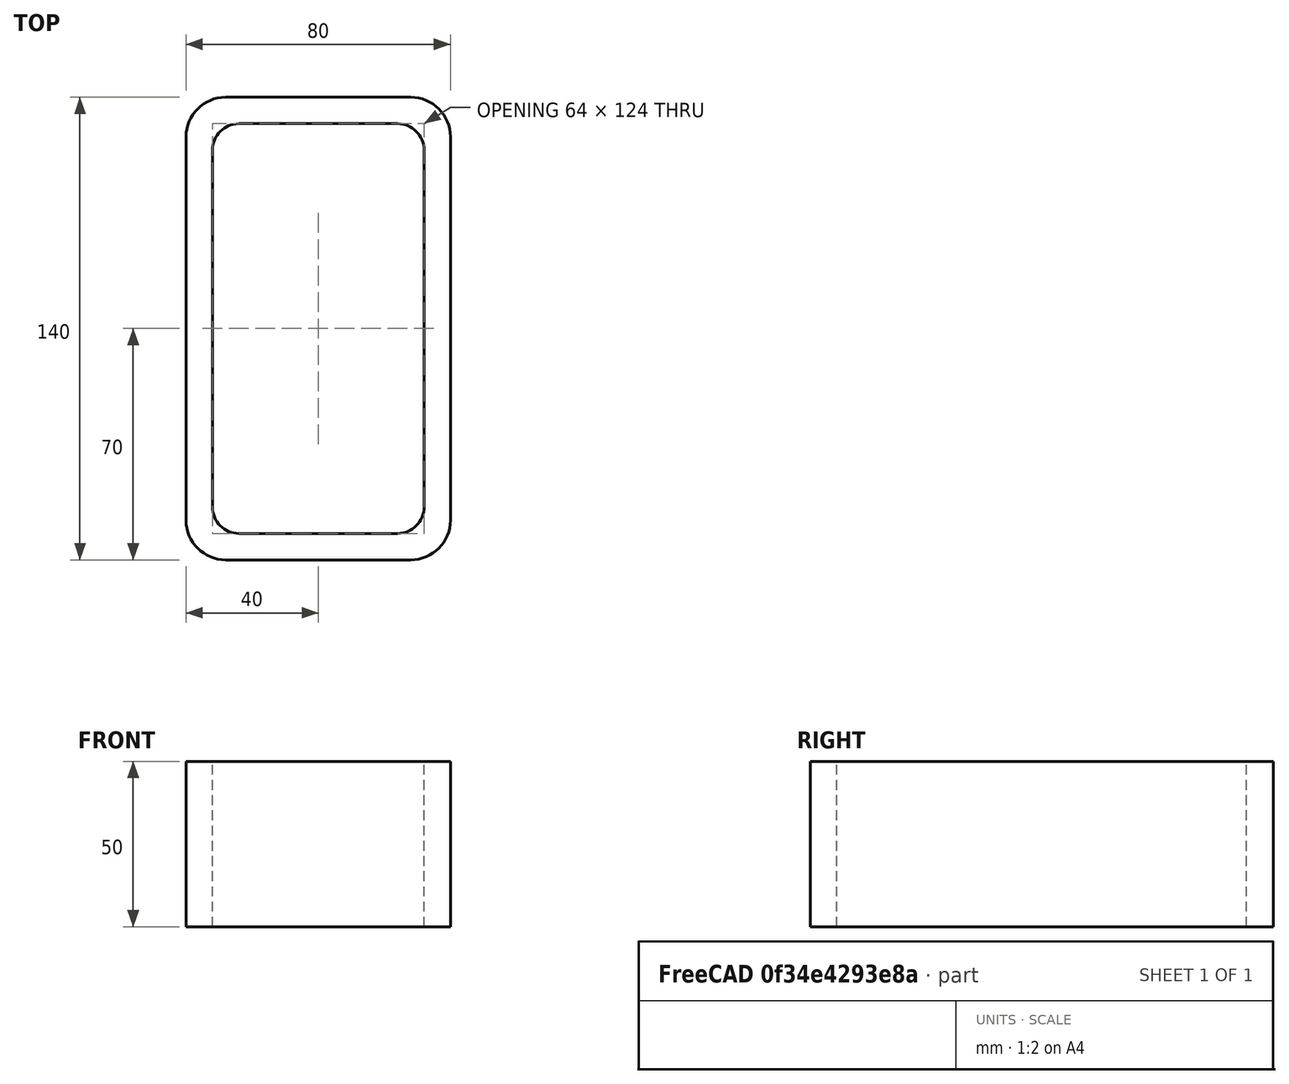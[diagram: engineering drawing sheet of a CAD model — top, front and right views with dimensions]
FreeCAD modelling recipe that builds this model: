
FCSTD DOCUMENT  (FreeCAD 0.15R4671 (Git))
Label: Rectangular hollow section 140x80x8 EN10219 S235JRH
License: All rights reserved
LicenseURL: http://en.wikipedia.org/wiki/All_rights_reserved
objects: Sketcher::SketchObject×1, Part::Extrusion×1
note: 2 computed .brp shape members not serialized (recipe doc carries the construction recipe); baked Part::Feature solids carry a one-line shape summary decoded from their .brp

FEATURE [Sketcher::SketchObject] Sketch
  sketch-geometry (16):
    g0: LineSegment StartX=-24 StartY=62 StartZ=0 EndX=24 EndY=62 EndZ=0
    g1: LineSegment StartX=32 StartY=54 StartZ=0 EndX=32 EndY=-54 EndZ=0
    g2: LineSegment StartX=24 StartY=-62 StartZ=0 EndX=-24 EndY=-62 EndZ=0
    g3: LineSegment StartX=-32 StartY=-54 StartZ=0 EndX=-32 EndY=54 EndZ=0
    g4: LineSegment StartX=-28 StartY=70 StartZ=0 EndX=28 EndY=70 EndZ=0
    g5: LineSegment StartX=40 StartY=58 StartZ=0 EndX=40 EndY=-58 EndZ=0
    g6: LineSegment StartX=28 StartY=-70 StartZ=0 EndX=-28 EndY=-70 EndZ=0
    g7: LineSegment StartX=-40 StartY=-58 StartZ=0 EndX=-40 EndY=58 EndZ=0
    g8: ArcOfCircle CenterX=-24 CenterY=54 CenterZ=0 NormalX=0 NormalY=0 NormalZ=1 Radius=8 StartAngle=1.5708 EndAngle=3.14159
    g9: ArcOfCircle CenterX=24 CenterY=54 CenterZ=0 NormalX=0 NormalY=0 NormalZ=1 Radius=8 StartAngle=0 EndAngle=1.5708
    g10: ArcOfCircle CenterX=24 CenterY=-54 CenterZ=0 NormalX=0 NormalY=0 NormalZ=1 Radius=8 StartAngle=4.71239 EndAngle=6.28319
    g11: ArcOfCircle CenterX=-24 CenterY=-54 CenterZ=0 NormalX=0 NormalY=0 NormalZ=1 Radius=8 StartAngle=3.14159 EndAngle=4.71239
    g12: ArcOfCircle CenterX=28 CenterY=58 CenterZ=0 NormalX=0 NormalY=0 NormalZ=1 Radius=12 StartAngle=0 EndAngle=1.5708
    g13: ArcOfCircle CenterX=28 CenterY=-58 CenterZ=0 NormalX=0 NormalY=0 NormalZ=1 Radius=12 StartAngle=4.71239 EndAngle=6.28319
    g14: ArcOfCircle CenterX=-28 CenterY=-58 CenterZ=0 NormalX=0 NormalY=0 NormalZ=1 Radius=12 StartAngle=3.14159 EndAngle=4.71239
    g15: ArcOfCircle CenterX=-28 CenterY=58 CenterZ=0 NormalX=0 NormalY=0 NormalZ=1 Radius=12 StartAngle=1.5708 EndAngle=3.14159
  constraints (36):
    c: Horizontal(g2)
    c: Vertical(g3)
    c: Horizontal(g6)
    c: Vertical(g7)
    c: Tangent(g3,g8) = 1.5708
    c: Tangent(g0,g8) = 1.5708
    c: Tangent(g0,g9) = 1.5708
    c: Tangent(g1,g9) = 1.5708
    c: Tangent(g1,g10) = 1.5708
    c: Tangent(g2,g10) = 1.5708
    c: Tangent(g2,g11) = 1.5708
    c: Tangent(g3,g11) = 1.5708
    c: Tangent(g4,g12) = 1.5708
    c: Tangent(g5,g12) = 1.5708
    c: Tangent(g5,g13) = 1.5708
    c: Tangent(g6,g13) = 1.5708
    c: Tangent(g6,g14) = 1.5708
    c: Tangent(g7,g14) = 1.5708
    c: Tangent(g7,g15) = 1.5708
    c: Tangent(g4,g15) = 1.5708
    c: Equal(g9,g8)
    c: Equal(g9,g11)
    c: Equal(g9,g10)
    c: Equal(g12,g15)
    c: Equal(g12,g14)
    c: Equal(g12,g13)
    c: Symmetric(g4,g6,g-1)
    c: Symmetric(g7,g5,g-2)
    c: DistanceY(g4,g6) = -140
    c: DistanceX(g7,g5) = 80
    c: Symmetric(g3,g1,g-2)
    c: Symmetric(g0,g2,g-1)
    c: DistanceY(g0,g4) = 8
    c: DistanceX(g5,g1) = -8
    c: Radius(g9) = 8
    c: Radius(g12) = 12
FEATURE [Part::Extrusion] Extrude  label="Rectangular hollow section 140x80x8 EN10219 S235JRH"
  Base = -> Sketch
  Dir = (0,0,50)
  Solid = true
